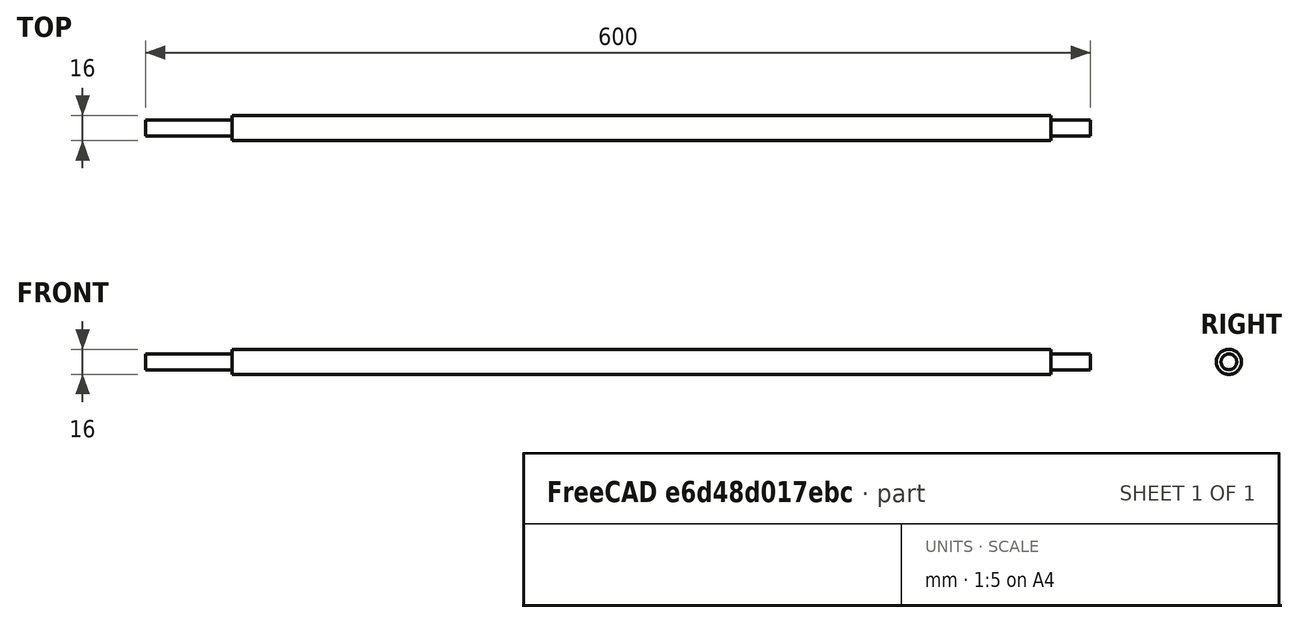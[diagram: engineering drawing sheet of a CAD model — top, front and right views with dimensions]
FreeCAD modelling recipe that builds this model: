
FCSTD DOCUMENT  (FreeCAD 0.21R33771 (Git))
Label: ViteCarro16x4
License: All rights reserved
LicenseURL: http://en.wikipedia.org/wiki/All_rights_reserved
objects: Sketcher::SketchObject×1, PartDesign::CoordinateSystem×1, PartDesign::Revolution×1, PartDesign::Body×1
note: 5 computed .brp shape members not serialized (recipe doc carries the construction recipe); baked Part::Feature solids carry a one-line shape summary decoded from their .brp

FEATURE [Sketcher::SketchObject] Sketch
  FullyConstrained = true
  MapMode = 5
  Support = -> [XY_Plane]
  sketch-geometry (8):
    g0: LineSegment StartX=0 StartY=0 StartZ=0 EndX=0 EndY=5 EndZ=0
    g1: LineSegment StartX=0 StartY=5 StartZ=0 EndX=55 EndY=5 EndZ=0
    g2: LineSegment StartX=55 StartY=5 StartZ=0 EndX=55 EndY=8 EndZ=0
    g3: LineSegment StartX=55 StartY=8 StartZ=0 EndX=575 EndY=8 EndZ=0
    g4: LineSegment StartX=575 StartY=8 StartZ=0 EndX=575 EndY=5 EndZ=0
    g5: LineSegment StartX=575 StartY=5 StartZ=0 EndX=600 EndY=5 EndZ=0
    g6: LineSegment StartX=600 StartY=5 StartZ=0 EndX=600 EndY=0 EndZ=0
    g7: LineSegment StartX=600 StartY=0 StartZ=0 EndX=0 EndY=0 EndZ=0
  constraints (23):
    c: Coincident(g0,g-1)
    c: PointOnObject(g0,g-2)
    c: Coincident(g1,g0)
    c: Horizontal(g1)
    c: Coincident(g2,g1)
    c: Vertical(g2)
    c: Coincident(g3,g2)
    c: Horizontal(g3)
    c: Coincident(g4,g3)
    c: Vertical(g4)
    c: Coincident(g5,g4)
    c: Horizontal(g5)
    c: Coincident(g6,g5)
    c: PointOnObject(g6,g-1)
    c: Vertical(g6)
    c: Coincident(g7,g6)
    c: Coincident(g7,g0)
    c: DistanceY(g0,g0) = 5
    c: DistanceY(g2,g2) = 3
    c: Equal(g2,g4)
    c: DistanceX(g3,g3) = 520
    c: DistanceX(g7,g7) = 600
    c: DistanceX(g5,g5) = 25
FEATURE [PartDesign::CoordinateSystem] LCS_ViteCarro16x4
  AttacherType = Attacher::AttachEngine3D
FEATURE [PartDesign::Revolution] Revolution
  Angle = 360
  Axis = (1,0,0)
  Base = (0,0,0)
  Profile = -> Sketch
  ReferenceAxis = -> Sketch [H_Axis]
FEATURE [PartDesign::Body] Body
  Group = -> [Sketch,LCS_ViteCarro16x4,Revolution]
  Origin = -> Origin
  Tip = -> Revolution
